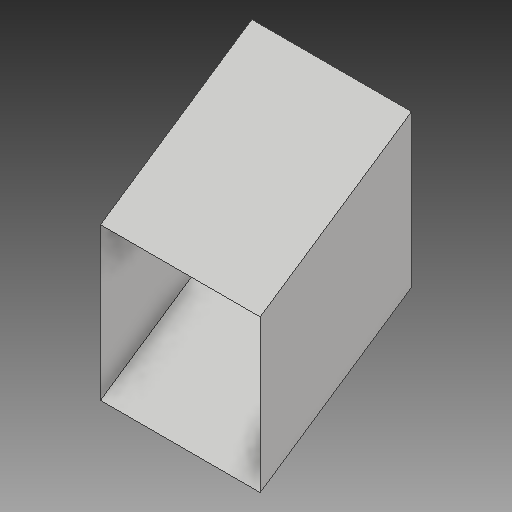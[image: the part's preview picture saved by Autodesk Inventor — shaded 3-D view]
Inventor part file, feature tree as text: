
AUTODESK INVENTOR PART (.ipt)
format: ipt  version: 2017 (Build 210142000, 142)  size: 92,160 bytes
history: native  units: in
note: dims shown in document units (in); Inventor stores cm internally (conversion verified against a paired STEP export)
features: sketch x2, sweep x1, other x1
ambient origin geometry x8: Origin, YZ Plane, XZ Plane, XY Plane, X Axis, Y Axis, Z Axis, Center Point
bodies: Solid1 (feature_tree)
feature tree (4):
  sweep  "ramp"
  other  "removed ends"
  sketch  "Sketch1"  dims[d0=7.0in d1=6.6667in]
  sketch  "Sketch2"  dims[d2=0.8521in d3=8.0in d4=0.0in d5=0.0in]
